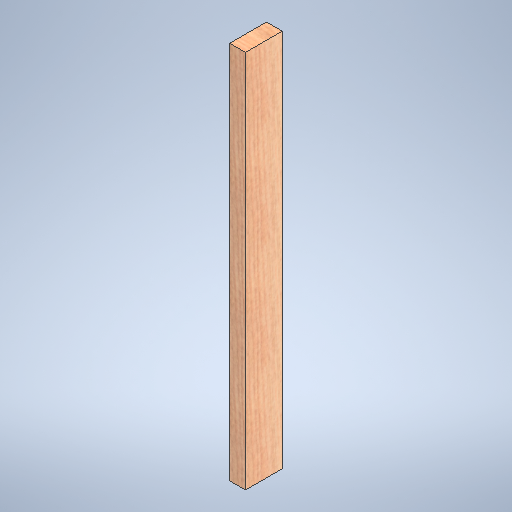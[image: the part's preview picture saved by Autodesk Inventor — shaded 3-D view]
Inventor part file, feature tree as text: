
AUTODESK INVENTOR PART (.ipt)
format: ipt  version: 2025.1 (Build 291241020, 241B)  size: 317,952 bytes
history: native  units: in
note: dims shown in document units (in); Inventor stores cm internally (conversion verified against a paired STEP export)
features: extrude x1, sketch x1
ambient origin geometry x8: Origin, YZ Plane, XZ Plane, XY Plane, X Axis, Y Axis, Z Axis, Center Point
bodies: Solid1 (feature_tree)
feature tree (2):
  extrude  "Extrusion1"  Depth=1.5in
  sketch  "Sketch1"  dims[d0=3.5in d1=1.5in d2=36.0in d3=0.0in]
